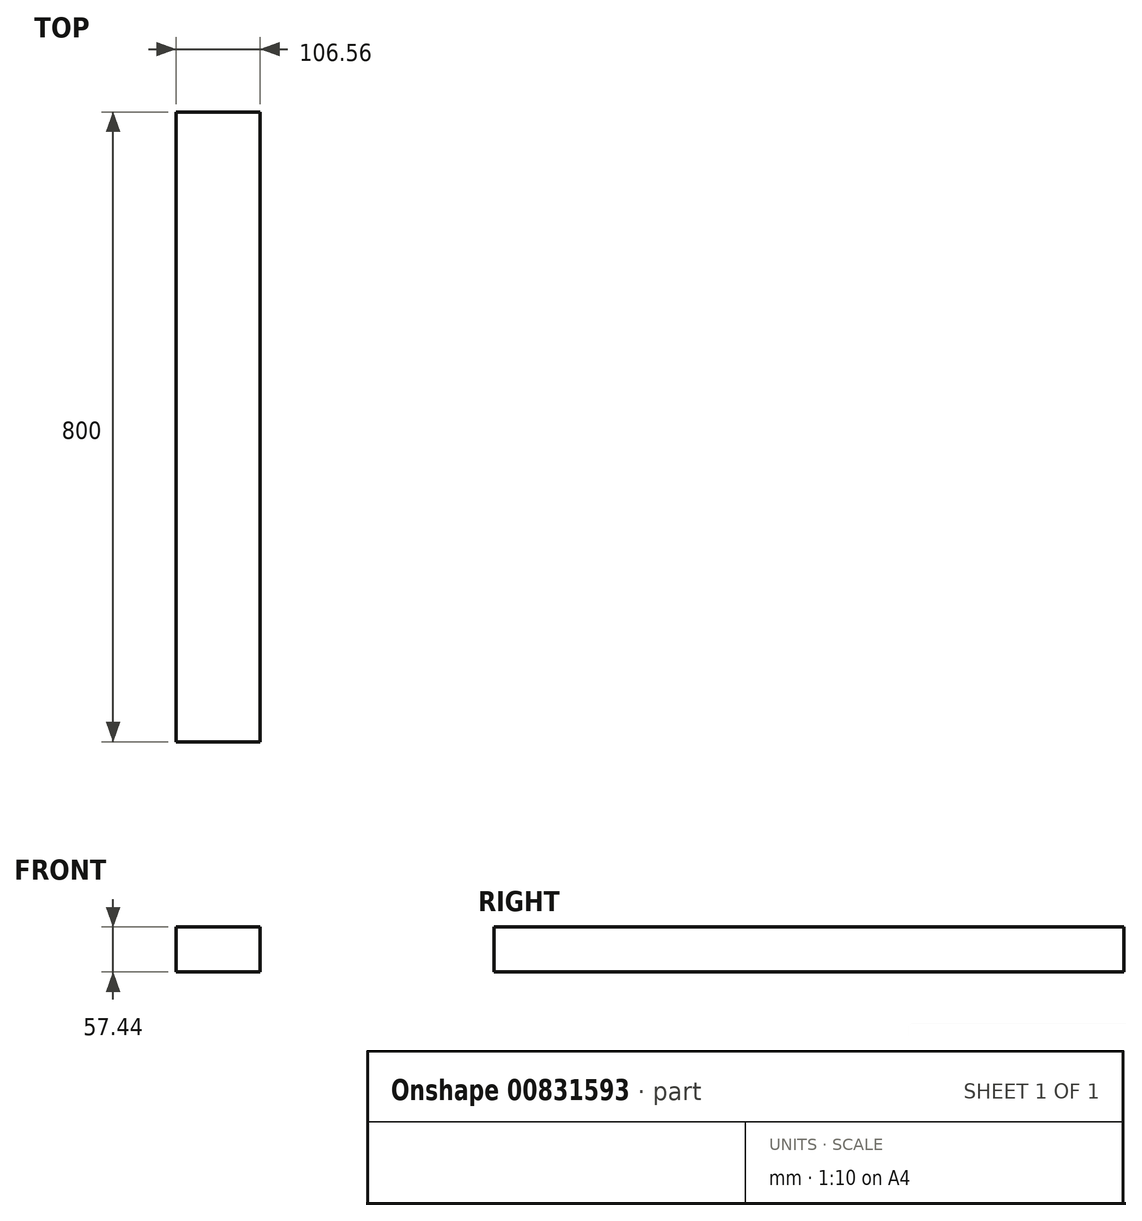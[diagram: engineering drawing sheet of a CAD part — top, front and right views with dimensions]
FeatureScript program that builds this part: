
annotation { "Feature Type Name" : "Feature", "Feature Type Description" : "" }
export const myFeature = defineFeature(function(context is Context, id is Id, definition is map)
    precondition{}
    {
        {
            var Q0;
            Q0=qCreatedBy(makeId("Front.planeOp"),FACE);
            var sketch = newSketch(context, id + "F0", { "sketchPlane" : qUnion([Q0])});
            skLineSegment(sketch, "E0.bottom", {"start": v(-53.28, 28.72) * mm, "end": v(53.28, 28.72) * mm});
            skLineSegment(sketch, "E0.top", {"start": v(-53.28, -28.72) * mm, "end": v(53.28, -28.72) * mm});
            skLineSegment(sketch, "E0.left", {"start": v(-53.28, 28.72) * mm, "end": v(-53.28, -28.72) * mm});
            skLineSegment(sketch, "E0.right", {"start": v(53.28, 28.72) * mm, "end": v(53.28, -28.72) * mm});
            skPoint(sketch, "E0.middle", {"position": v(0, 0) * mm});
            skSolve(sketch);
        }
        {
            var Q0;
            Q0=makeQuery(id+"F0.imprint","IMPRINT",FACE,{"disambiguationData":[TD([[makeQuery(id+"F0.imprint","IMPRINT",EDGE,{"derivedFrom":sQuery(id+"F0.wireOp",EDGE,"E0.bottom")}),-1.0]])]});
            extrude(context, id + "F1", {"entities" : qUnion([Q0]), "endBound" : BoundingType.SYMMETRIC, "depth" : 800 * mm, "offsetDistance" : 25.4 * mm});
        }
    });
